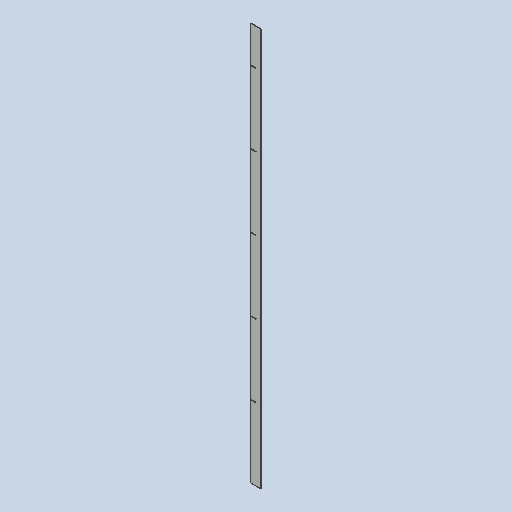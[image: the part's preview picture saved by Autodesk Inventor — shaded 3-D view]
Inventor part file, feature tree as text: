
AUTODESK INVENTOR PART (.ipt)
format: ipt  version: 2025 (Build 290162010, 162A)  size: 148,480 bytes
history: native  units: mm
features: other x3, sketch x2, sheet_metal_op x1, extrude x1, pattern_linear x1, projected_geometry x1
ambient origin geometry x8: Origin, YZ Plane, XZ Plane, XY Plane, X Axis, Y Axis, Z Axis, Center Point
bodies: Body1 (feature_tree)
feature tree (9):
  other  "BSH 043 stringer 3"
  sheet_metal_op  "Face2"
  extrude  "Extrusion2"  Depth=2751.5mm
  pattern_linear  "Rectangular Pattern1"  Spacing1=36.235469mm  [1 undecoded]
  sketch  "Sketch6"  dims[d26=70.470938mm d27=2751.5mm]
  other  "Plate4"
  sketch  "Sketch7"  dims[d28=3.0mm d29=36.235469mm d30=3.2mm d31=498.5mm d32=0.0mm d33=0.0mm d34=50.0mm d36=500.0mm]
  projected_geometry  "Projected Loop1"
  other  "Definition1"
note: 1 required parameter value undecoded (feature->parameter linkage not recoverable at this tier; creation-order binding heuristic only, values carry confidence <= 0.55)
